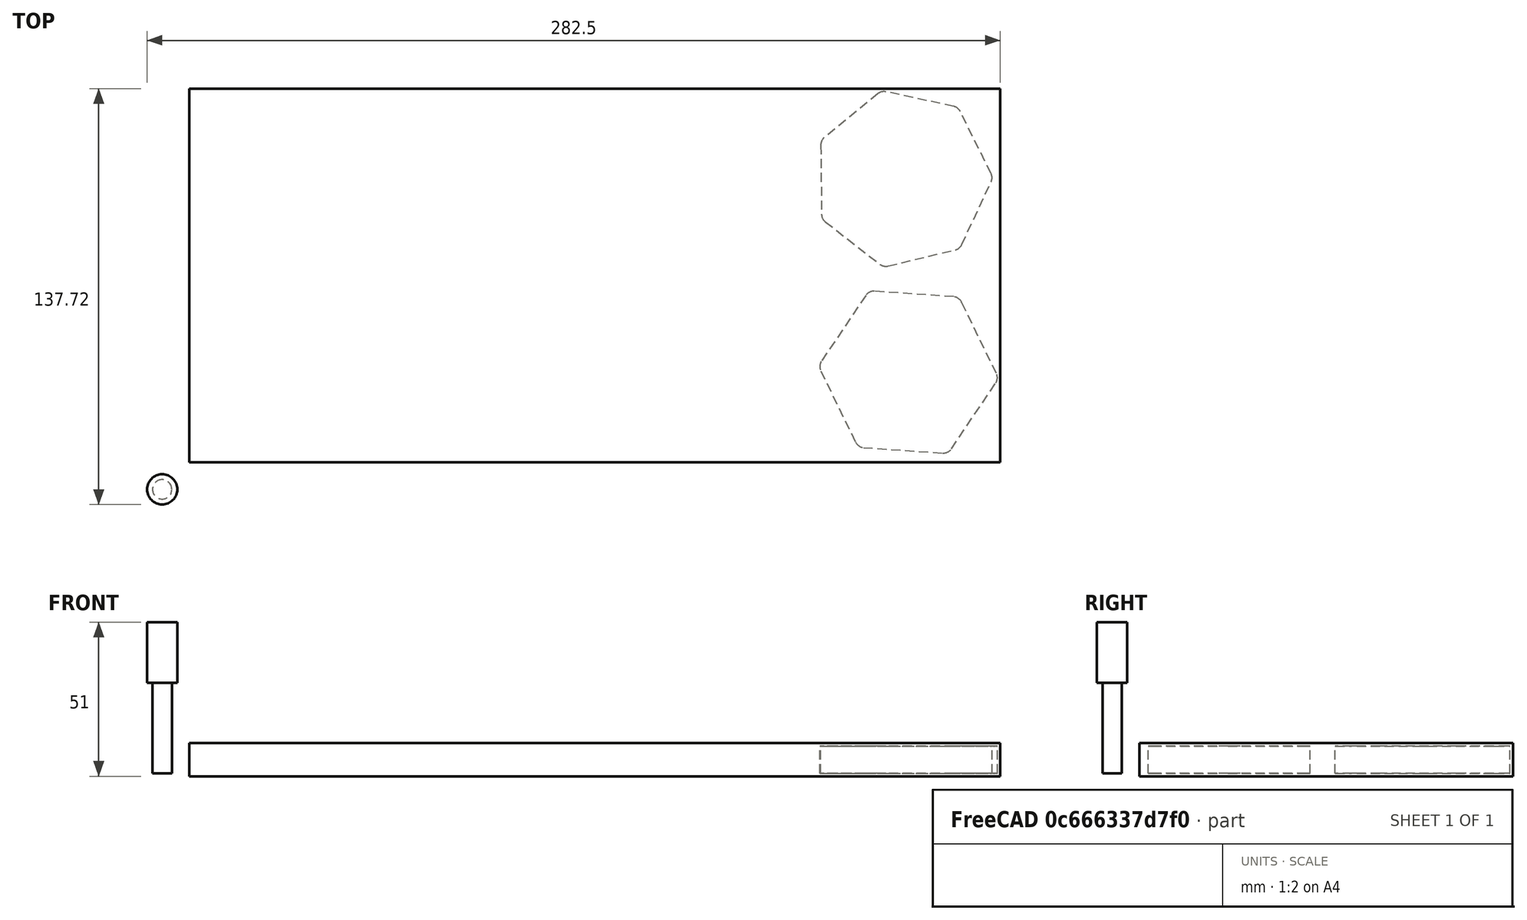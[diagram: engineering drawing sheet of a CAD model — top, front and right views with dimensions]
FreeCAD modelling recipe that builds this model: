
FCSTD DOCUMENT  (FreeCAD 0.20R27770 (Git))
Label: Demo2Spread
License: All rights reserved
LicenseURL: http://en.wikipedia.org/wiki/All_rights_reserved
objects: Part::FeaturePython×6, Path::FeaturePython×4, Sketcher::SketchObject×3, PartDesign::Pad×3, PartDesign::Fillet×3, PartDesign::Body×3, App::DocumentObjectGroup×2, Spreadsheet::Sheet×1, App::FeaturePython×1, Path::FeatureCompoundPython×1, Mesh::FeaturePython×1
note: 26 computed .brp shape members not serialized (recipe doc carries the construction recipe); baked Part::Feature solids carry a one-line shape summary decoded from their .brp

FEATURE [Spreadsheet::Sheet] Spreadsheet
  cells = A1=Length; B1(Length)=200; A2=Height; B2(Height)=120; A3=Thickness; B3(Thickness)=9; A5=Octogon; B5(Octagon)=60; A6=Septagon; B6(Septagon)=60; A7=Hexagon; B7(Hexagon)=60; A10=Border; B10(Border)=10
FEATURE [Sketcher::SketchObject] Sketch
  FullyConstrained = false
  MapMode = 5
  Support = -> [XY_Plane]
  expr: Constraints[10] = <<Spreadsheet>>.Border
  expr: Constraints[11] = <<Spreadsheet>>.Border
  expr: Constraints[72] = <<Spreadsheet>>.Octagon
  expr: Constraints[73] = <<Spreadsheet>>.Septagon
  expr: Constraints[74] = <<Spreadsheet>>.Hexagon
  expr: Constraints[75] = <<Spreadsheet>>.Octagon / 2 + <<Spreadsheet>>.Border
  expr: Constraints[76] = <<Spreadsheet>>.Octagon / 2 + <<Spreadsheet>>.Border
  expr: Constraints[77] = <<Spreadsheet>>.Septagon / 2 + <<Spreadsheet>>.Border
  expr: Constraints[78] = <<Spreadsheet>>.Hexagon / 2 + <<Spreadsheet>>.Border
  expr: Constraints[79] = <<Spreadsheet>>.Hexagon / 2 + <<Spreadsheet>>.Border
  expr: Constraints[80] = <<Spreadsheet>>.Length / 2
  expr: Constraints[8] = <<Spreadsheet>>.Length
  expr: Constraints[9] = <<Spreadsheet>>.Height
  sketch-geometry (28):
    g0: LineSegment StartX=10 StartY=130 StartZ=0 EndX=210 EndY=130 EndZ=0
    g1: LineSegment StartX=210 StartY=130 StartZ=0 EndX=210 EndY=10 EndZ=0
    g2: LineSegment StartX=210 StartY=10 StartZ=0 EndX=10 EndY=10 EndZ=0
    g3: LineSegment StartX=10 StartY=10 StartZ=0 EndX=10 EndY=130 EndZ=0
    g4: LineSegment StartX=72.0257 StartY=29.6317 StartZ=0 EndX=79.9771 EndY=51.172 EndZ=0
    g5: LineSegment StartX=79.9771 StartY=51.172 StartZ=0 EndX=70.3683 EndY=72.0257 EndZ=0
    g6: LineSegment StartX=70.3683 StartY=72.0257 StartZ=0 EndX=48.828 EndY=79.9771 EndZ=0
    g7: LineSegment StartX=48.828 StartY=79.9771 StartZ=0 EndX=27.9743 EndY=70.3683 EndZ=0
    g8: LineSegment StartX=27.9743 StartY=70.3683 StartZ=0 EndX=20.0229 EndY=48.828 EndZ=0
    g9: LineSegment StartX=20.0229 StartY=48.828 StartZ=0 EndX=29.6317 EndY=27.9743 EndZ=0
    g10: LineSegment StartX=29.6317 StartY=27.9743 StartZ=0 EndX=51.172 EndY=20.0229 EndZ=0
    g11: LineSegment StartX=51.172 StartY=20.0229 StartZ=0 EndX=72.0257 EndY=29.6317 EndZ=0
    g12: Circle CenterX=50 CenterY=50 CenterZ=0 NormalX=0 NormalY=0 NormalZ=1 AngleXU=0 Radius=30
    g13: LineSegment StartX=117.529 StartY=60.9602 StartZ=0 EndX=137.399 EndY=77.7807 EndZ=0
    g14: LineSegment StartX=137.399 StartY=77.7807 StartZ=0 EndX=136.636 EndY=103.803 EndZ=0
    g15: LineSegment StartX=136.636 StartY=103.803 StartZ=0 EndX=115.816 EndY=119.431 EndZ=0
    g16: LineSegment StartX=115.816 StartY=119.431 StartZ=0 EndX=90.6164 EndY=112.897 EndZ=0
    g17: LineSegment StartX=90.6164 StartY=112.897 StartZ=0 EndX=80.0129 EndY=89.1214 EndZ=0
    g18: LineSegment StartX=80.0129 StartY=89.1214 StartZ=0 EndX=91.9903 EndY=66.0073 EndZ=0
    g19: LineSegment StartX=91.9903 StartY=66.0073 StartZ=0 EndX=117.529 EndY=60.9602 EndZ=0
    g20: Circle CenterX=110 CenterY=90 CenterZ=0 NormalX=0 NormalY=0 NormalZ=1 AngleXU=0 Radius=30
    g21: LineSegment StartX=179.76 StartY=21.632 StartZ=0 EndX=199.447 EndY=44.2684 EndZ=0
    g22: LineSegment StartX=199.447 StartY=44.2684 StartZ=0 EndX=189.687 EndY=72.6364 EndZ=0
    g23: LineSegment StartX=189.687 StartY=72.6364 StartZ=0 EndX=160.24 EndY=78.368 EndZ=0
    g24: LineSegment StartX=160.24 StartY=78.368 StartZ=0 EndX=140.553 EndY=55.7316 EndZ=0
    g25: LineSegment StartX=140.553 StartY=55.7316 StartZ=0 EndX=150.313 EndY=27.3636 EndZ=0
    g26: LineSegment StartX=150.313 StartY=27.3636 StartZ=0 EndX=179.76 EndY=21.632 EndZ=0
    g27: Circle CenterX=170 CenterY=50 CenterZ=0 NormalX=0 NormalY=0 NormalZ=1 AngleXU=0 Radius=30
  constraints (66):
    c: Coincident(g0,g1)
    c: Coincident(g1,g2)
    c: Coincident(g2,g3)
    c: Coincident(g3,g0)
    c: Horizontal(g0)
    c: Horizontal(g2)
    c: Vertical(g1)
    c: Vertical(g3)
    c: DistanceX(g2,g2) = 200
    c: DistanceY(g3,g3) = 120
    c: DistanceX(g-1,g2) = 10
    c: DistanceY(g-1,g2) = 10
    c: Coincident(g4,g5)
    c: Coincident(g5,g6)
    c: Coincident(g6,g7)
    c: Coincident(g7,g8)
    c: Coincident(g8,g9)
    c: Coincident(g9,g10)
    c: Coincident(g10,g11)
    c: Coincident(g11,g4)
    c: Equal(g4, g5-g11) x7
    c: PointOnObject(g4,g12)
    c: PointOnObject(g5,g12)
    c: PointOnObject(g6,g12)
    c: PointOnObject(g7,g12)
    c: PointOnObject(g8,g12)
    c: PointOnObject(g9,g12)
    c: PointOnObject(g10,g12)
    c: PointOnObject(g11,g12)
    c: Coincident(g13,g14)
    c: Coincident(g14,g15)
    c: Coincident(g15,g16)
    c: Coincident(g16,g17)
    c: Coincident(g17,g18)
    c: Coincident(g18,g19)
    c: Coincident(g19,g13)
    c: Equal(g13, g14-g19) x6
    c: PointOnObject(g13,g20)
    c: PointOnObject(g14,g20)
    c: PointOnObject(g15,g20)
    c: PointOnObject(g16,g20)
    c: PointOnObject(g17,g20)
    c: PointOnObject(g18,g20)
    c: PointOnObject(g19,g20)
    c: Coincident(g21,g22)
    c: Coincident(g22,g23)
    c: Coincident(g23,g24)
    c: Coincident(g24,g25)
    c: Coincident(g25,g26)
    c: Coincident(g26,g21)
    c: Equal(g21, g22-g26) x5
    c: PointOnObject(g21,g27)
    c: PointOnObject(g22,g27)
    c: PointOnObject(g23,g27)
    c: PointOnObject(g24,g27)
    c: PointOnObject(g25,g27)
    c: PointOnObject(g26,g27)
    c: Diameter(g12) = 60
    c: Diameter(g20) = 60
    c: Diameter(g27) = 60
    c: DistanceX(g2,g12) = 40
    c: DistanceY(g2,g12) = 40
    c: DistanceY(g20,g0) = 40
    c: DistanceY(g1,g27) = 40
    c: DistanceX(g27,g1) = 40
    c: DistanceX(g2,g20) = 100
FEATURE [PartDesign::Pad] Pad
  Direction = (0,0,1)
  Length = 9
  Length2 = 10
  Profile = -> Sketch
  ReferenceAxis = -> Sketch [N_Axis]
  Type = 0
FEATURE [Sketcher::SketchObject] Sketch001
  FullyConstrained = false
  MapMode = 5
  Support = -> [XY_Plane001]
  expr: Constraints[17] = <<Spreadsheet>>.Hexagon - 0.1
  sketch-geometry (7):
    g0: LineSegment StartX=276.987 StartY=36.7305 StartZ=0 EndX=263.85 EndY=63.6453 EndZ=0
    g1: LineSegment StartX=263.85 StartY=63.6453 StartZ=0 EndX=233.972 EndY=65.7254 EndZ=0
    g2: LineSegment StartX=233.972 StartY=65.7254 StartZ=0 EndX=217.232 EndY=40.8906 EndZ=0
    g3: LineSegment StartX=217.232 StartY=40.8906 StartZ=0 EndX=230.369 EndY=13.9758 EndZ=0
    g4: LineSegment StartX=230.369 StartY=13.9758 StartZ=0 EndX=260.247 EndY=11.8957 EndZ=0
    g5: LineSegment StartX=260.247 StartY=11.8957 StartZ=0 EndX=276.987 EndY=36.7305 EndZ=0
    g6: Circle CenterX=247.109 CenterY=38.8105 CenterZ=0 NormalX=0 NormalY=0 NormalZ=1 AngleXU=0 Radius=29.95
  constraints (14):
    c: Coincident(g0,g1)
    c: Coincident(g1,g2)
    c: Coincident(g2,g3)
    c: Coincident(g3,g4)
    c: Coincident(g4,g5)
    c: Coincident(g5,g0)
    c: Equal(g0, g1-g5) x5
    c: PointOnObject(g0,g6)
    c: PointOnObject(g1,g6)
    c: PointOnObject(g2,g6)
    c: PointOnObject(g3,g6)
    c: PointOnObject(g4,g6)
    c: PointOnObject(g5,g6)
    c: Diameter(g6) = 59.9
FEATURE [PartDesign::Pad] Pad001
  Direction = (0,0,1)
  Length = 9
  Length2 = 10
  Profile = -> Sketch001
  ReferenceAxis = -> Sketch001 [N_Axis]
  Type = 0
FEATURE [Sketcher::SketchObject] Sketch002
  FullyConstrained = false
  MapMode = 5
  Support = -> [XY_Plane002]
  expr: Constraints[20] = <<Spreadsheet>>.Septagon - 0.1
  sketch-geometry (8):
    g0: LineSegment StartX=264.102 StartY=79.6641 StartZ=0 EndX=275.099 EndY=103.213 EndZ=0
    g1: LineSegment StartX=275.099 StartY=103.213 StartZ=0 EndX=263.544 EndY=126.492 EndZ=0
    g2: LineSegment StartX=263.544 StartY=126.492 StartZ=0 EndX=238.139 EndY=131.974 EndZ=0
    g3: LineSegment StartX=238.139 StartY=131.974 StartZ=0 EndX=218.014 EndY=115.528 EndZ=0
    g4: LineSegment StartX=218.014 StartY=115.528 StartZ=0 EndX=218.323 EndY=89.5407 EndZ=0
    g5: LineSegment StartX=218.323 StartY=89.5407 StartZ=0 EndX=238.834 EndY=73.5795 EndZ=0
    g6: LineSegment StartX=238.834 StartY=73.5795 StartZ=0 EndX=264.102 EndY=79.6641 EndZ=0
    g7: Circle CenterX=245.151 CenterY=102.856 CenterZ=0 NormalX=0 NormalY=0 NormalZ=1 AngleXU=0 Radius=29.95
  constraints (16):
    c: Coincident(g0,g1)
    c: Coincident(g1,g2)
    c: Coincident(g2,g3)
    c: Coincident(g3,g4)
    c: Coincident(g4,g5)
    c: Coincident(g5,g6)
    c: Coincident(g6,g0)
    c: Equal(g0, g1-g6) x6
    c: PointOnObject(g0,g7)
    c: PointOnObject(g1,g7)
    c: PointOnObject(g2,g7)
    c: PointOnObject(g3,g7)
    c: PointOnObject(g4,g7)
    c: PointOnObject(g5,g7)
    c: PointOnObject(g6,g7)
    c: Diameter(g7) = 59.9
FEATURE [PartDesign::Pad] Pad002
  Direction = (0,0,1)
  Length = 9
  Length2 = 10
  Profile = -> Sketch002
  ReferenceAxis = -> Sketch002 [N_Axis]
  Type = 0
FEATURE [PartDesign::Fillet] Fillet
  Base = -> Pad002 [Edge1,Edge17,Edge2,Edge14,Edge5,Edge8,Edge11]
  BaseFeature = -> Pad002
  Radius = 3.2
  SupportTransform = false
  UseAllEdges = false
FEATURE [PartDesign::Body] Body002  label="Heptagon"
  Group = -> [Sketch002,Pad002,Fillet]
  Origin = -> Origin002
  Tip = -> Fillet
FEATURE [PartDesign::Fillet] Fillet001
  Base = -> Pad [Edge58,Edge38,Edge37,Edge53,Edge13,Edge32,Edge29,Edge26,Edge23,Edge50,Edge47,Edge68,Edge71,Edge20,Edge17,Edge44,Edge65,Edge62,Edge41,Edge14,Edge59]
  BaseFeature = -> Pad
  Radius = 3.2
  SupportTransform = false
  UseAllEdges = false
FEATURE [PartDesign::Body] Body
  Group = -> [Sketch,Pad,Fillet001]
  Origin = -> Origin
  Tip = -> Fillet001
FEATURE [PartDesign::Fillet] Fillet002
  Base = -> Pad001 [Edge14,Edge11,Edge1,Edge2,Edge5,Edge8]
  BaseFeature = -> Pad001
  Radius = 3.2
  SupportTransform = false
  UseAllEdges = false
FEATURE [PartDesign::Body] Body001  label="Hexagon"
  Group = -> [Sketch001,Pad001,Fillet002]
  Origin = -> Origin001
  Tip = -> Fillet002
FEATURE [App::FeaturePython] SetupSheet  # Path/CAM operation (typed FeaturePython)
  ClearanceHeightExpression = OpStockZMax+SetupSheet.ClearanceHeightOffset
  ClearanceHeightOffset = 5
  CoolantMode = 0
  CoolantModes = None | Flood | Mist
  FinalDepthExpression = OpFinalDepth
  HorizRapid = 0
  SafeHeightExpression = OpStockZMax+SetupSheet.SafeHeightOffset
  SafeHeightOffset = 3
  StepDownExpression = OpToolDiameter
  VertRapid = 0
FEATURE [Part::FeaturePython] Clone  label="Model-Body"  # Draft clone (typed FeaturePython)
  AttacherType = Attacher::AttachEngine3D
  Fuse = false
  Objects = -> [Body]
  PathResource = Model
  Scale = (1,1,1)
FEATURE [Part::FeaturePython] Clone001  label="Model-Heptagon"  # Draft clone (typed FeaturePython)
  AttacherType = Attacher::AttachEngine3D
  Fuse = false
  Objects = -> [Body002]
  PathResource = Model
  Scale = (1,1,1)
FEATURE [Part::FeaturePython] Clone002  label="Model-Hexagon"  # Draft clone (typed FeaturePython)
  AttacherType = Attacher::AttachEngine3D
  Fuse = false
  Objects = -> [Body001]
  PathResource = Model
  Scale = (1,1,1)
FEATURE [App::DocumentObjectGroup] Model
  Group = -> [Clone,Clone001,Clone002]
FEATURE [Part::FeaturePython] Stock  # WARN: FeaturePython — macro-defined, semantics opaque (R4)
  Base = -> Model
  ExtXneg = 1
  ExtXpos = 1
  ExtYneg = 1
  ExtYpos = 1
  ExtZneg = 1
  ExtZpos = 1
  Placement = pos=(10,10,0) rot=(0,0,1;0rad)
  StockType = FromBase
FEATURE [Part::FeaturePython] ToolBit001  label="6.4mm Endmill"  # Path/CAM toolbit (typed FeaturePython)
  BitPropertyNames = Chipload | CuttingEdgeHeight | Diameter | Flutes | Length | Material | ShankDiameter
  BitShape = <path>
  Chipload = 0
  CuttingEdgeHeight = 30
  Diameter = 6.4
  File = <userpath>/MensShed/CNCRouter/FreeCAD/Bit/6.4mm_Endmill.fctb
  Flutes = 0
  Length = 50
  Material = 0
  ShankDiameter = 10
  ShapeName = endmill
FEATURE [Part::FeaturePython] ToolBit  label="6.4mm Endmill002"  # Path/CAM toolbit (typed FeaturePython)
  BitPropertyNames = Chipload | CuttingEdgeHeight | Diameter | Flutes | Length | Material | ShankDiameter
  BitShape = <path>
  Chipload = 0
  CuttingEdgeHeight = 30
  Diameter = 6.4
  Flutes = 0
  Length = 50
  Material = 0
  ShankDiameter = 10
  ShapeName = endmill
FEATURE [Path::FeaturePython] __4mm_Endmill  label="6.4mm Endmill001"  # Path/CAM operation (typed FeaturePython)
  HorizFeed = 10
  HorizRapid = 0
  SpindleDir = 1
  SpindleSpeed = 10000
  Tool = -> ToolBit
  ToolNumber = 2
  VertFeed = 10
  VertRapid = 0
  expr: HorizRapid = SetupSheet.HorizRapid
  expr: VertRapid = SetupSheet.VertRapid
FEATURE [App::DocumentObjectGroup] Tools
  Group = -> [__4mm_Endmill]
FEATURE [Path::FeaturePython] Profile  label="Holes"  # Path/CAM operation (typed FeaturePython)
  Active = true
  AreaParams:
    Tolerance = 1e-07
    FitArcs = True
    Simplify = False
    CleanDistance = 0.0
    Accuracy = 0.01
    Unit = 1.0
    MinArcPoints = 4
    MaxArcPoints = 100
    ClipperScale = 10000000.0
    Fill = 0
    Coplanar = 0
    Reorient = True
    Outline = False
    Explode = False
    OpenMode = 0
    Deflection = 0.01
    SubjectFill = 0
    ClipFill = 0
    Offset = -3.2
    ExtraPass = 0
    Stepover = 0.0
    LastStepover = 0.0
    JoinType = 0
    EndType = 0
    MiterLimit = 2.0
    RoundPrecision = 0.0
    PocketMode = 0
    ToolRadius = 1.0
    PocketExtraOffset = 0.0
    PocketStepover = 0.0
    PocketLastStepover = 0.0
    FromCenter = False
    Angle = 45.0
    AngleShift = 0.0
    Shift = 0.0
    Thicken = False
    SectionCount = -1
    Stepdown = 1.0
    SectionOffset = 0.0
    SectionTolerance = 1e-06
    SectionMode = 2
    Project = False
  Base = -> [Clone]
  ClearanceHeight = 15
  CoolantMode = 0
  CycleTime = 00:02:52
  Direction = 0
  FinalDepth = 0.01
  HandleMultipleFeatures = 0
  JoinType = 0
  MiterLimit = 0.1
  OffsetExtra = 0
  OpFinalDepth = 9
  OpStartDepth = 10
  OpStockZMax = 10
  OpStockZMin = -1
  OpToolDiameter = 6.4
  PathParams = {'orientation': 1, 'feedrate': 10.0, 'feedrate_v': 10.0, 'verbose': True, 'resume_height': 13.0, 'retraction': 15.0, 'return_end': True, 'preamble': False, 'start': Vector (88.35010162148484, 79.98736022550277, 15.0)}
  SafeHeight = 13
  Side = 1
  SplitArcs = false
  StartDepth = 9
  StartPoint = (0,0,0)
  StepDown = 3
  ToolController = -> __4mm_Endmill
  UseComp = true
  UseStartPoint = false
  processCircles = false
  processHoles = false
  processPerimeter = true
  expr: ClearanceHeight = OpStockZMax + SetupSheet.ClearanceHeightOffset
  expr: FinalDepth = 0.01
  expr: SafeHeight = OpStockZMax + SetupSheet.SafeHeightOffset
  expr: StartDepth = <<Spreadsheet>>.Thickness
  expr: StepDown = 3
FEATURE [Path::FeaturePython] Profile001  # Path/CAM operation (typed FeaturePython)
  Active = true
  AreaParams:
    Tolerance = 1e-07
    FitArcs = True
    Simplify = False
    CleanDistance = 0.0
    Accuracy = 0.01
    Unit = 1.0
    MinArcPoints = 4
    MaxArcPoints = 100
    ClipperScale = 10000000.0
    Fill = 0
    Coplanar = 0
    Reorient = True
    Outline = False
    Explode = False
    OpenMode = 0
    Deflection = 0.01
    SubjectFill = 0
    ClipFill = 0
    Offset = 3.2
    ExtraPass = 0
    Stepover = 0.0
    LastStepover = 0.0
    JoinType = 0
    EndType = 0
    MiterLimit = 2.0
    RoundPrecision = 0.0
    PocketMode = 0
    ToolRadius = 1.0
    PocketExtraOffset = 0.0
    PocketStepover = 0.0
    PocketLastStepover = 0.0
    FromCenter = False
    Angle = 45.0
    AngleShift = 0.0
    Shift = 0.0
    Thicken = False
    SectionCount = -1
    Stepdown = 1.0
    SectionOffset = 0.0
    SectionTolerance = 1e-06
    SectionMode = 2
    Project = False
  ClearanceHeight = 15
  CoolantMode = 0
  CycleTime = 00:05:50
  Direction = 0
  FinalDepth = 0.01
  HandleMultipleFeatures = 0
  JoinType = 0
  MiterLimit = 0.1
  OffsetExtra = 0
  OpFinalDepth = -1
  OpStartDepth = 10
  OpStockZMax = 10
  OpStockZMin = -1
  OpToolDiameter = 6.4
  PathParams = {'orientation': 1, 'feedrate': 10.0, 'feedrate_v': 10.0, 'verbose': True, 'resume_height': 13.0, 'retraction': 15.0, 'return_end': True, 'preamble': False, 'start': Vector (220.74846266977696, 121.88629926680255, 15.0)}
  SafeHeight = 13
  Side = 0
  SplitArcs = false
  StartDepth = 9
  StartPoint = (0,0,0)
  StepDown = 3
  ToolController = -> __4mm_Endmill
  UseComp = true
  UseStartPoint = false
  processCircles = false
  processHoles = false
  processPerimeter = true
  expr: ClearanceHeight = OpStockZMax + SetupSheet.ClearanceHeightOffset
  expr: FinalDepth = 0.01
  expr: SafeHeight = OpStockZMax + SetupSheet.SafeHeightOffset
  expr: StartDepth = <<Spreadsheet>>.Thickness
  expr: StepDown = 3
FEATURE [Path::FeatureCompoundPython] Operations  # Path/CAM operation (typed FeaturePython)
  Group = -> [Profile,Profile001]
  UsePlacements = false
FEATURE [Path::FeaturePython] Job  # Path/CAM operation (typed FeaturePython)
  CycleTime = 00:08:42
  Fixtures = G54
  GeometryTolerance = 0.01
  JobType = 0
  LastPostProcessDate = 2022-02-28 10:54:35.296858
  LastPostProcessOutput = <userpath>/MensShed/CNCRouter/Shapes/Demo2Spread.ngc
  Model = -> Model
  Operations = -> Operations
  OrderOutputBy = 0
  PostProcessor = 7
  PostProcessorOutputFile = %D/%d.ngc
  SetupSheet = -> SetupSheet
  SplitOutput = false
  Stock = -> Stock
  Tools = -> Tools
FEATURE [Mesh::FeaturePython] CutMaterial  # WARN: FeaturePython — macro-defined, semantics opaque (R4)
note: 2 file-system paths scrubbed to <path> (originals preserved in the JSON sidecar)
